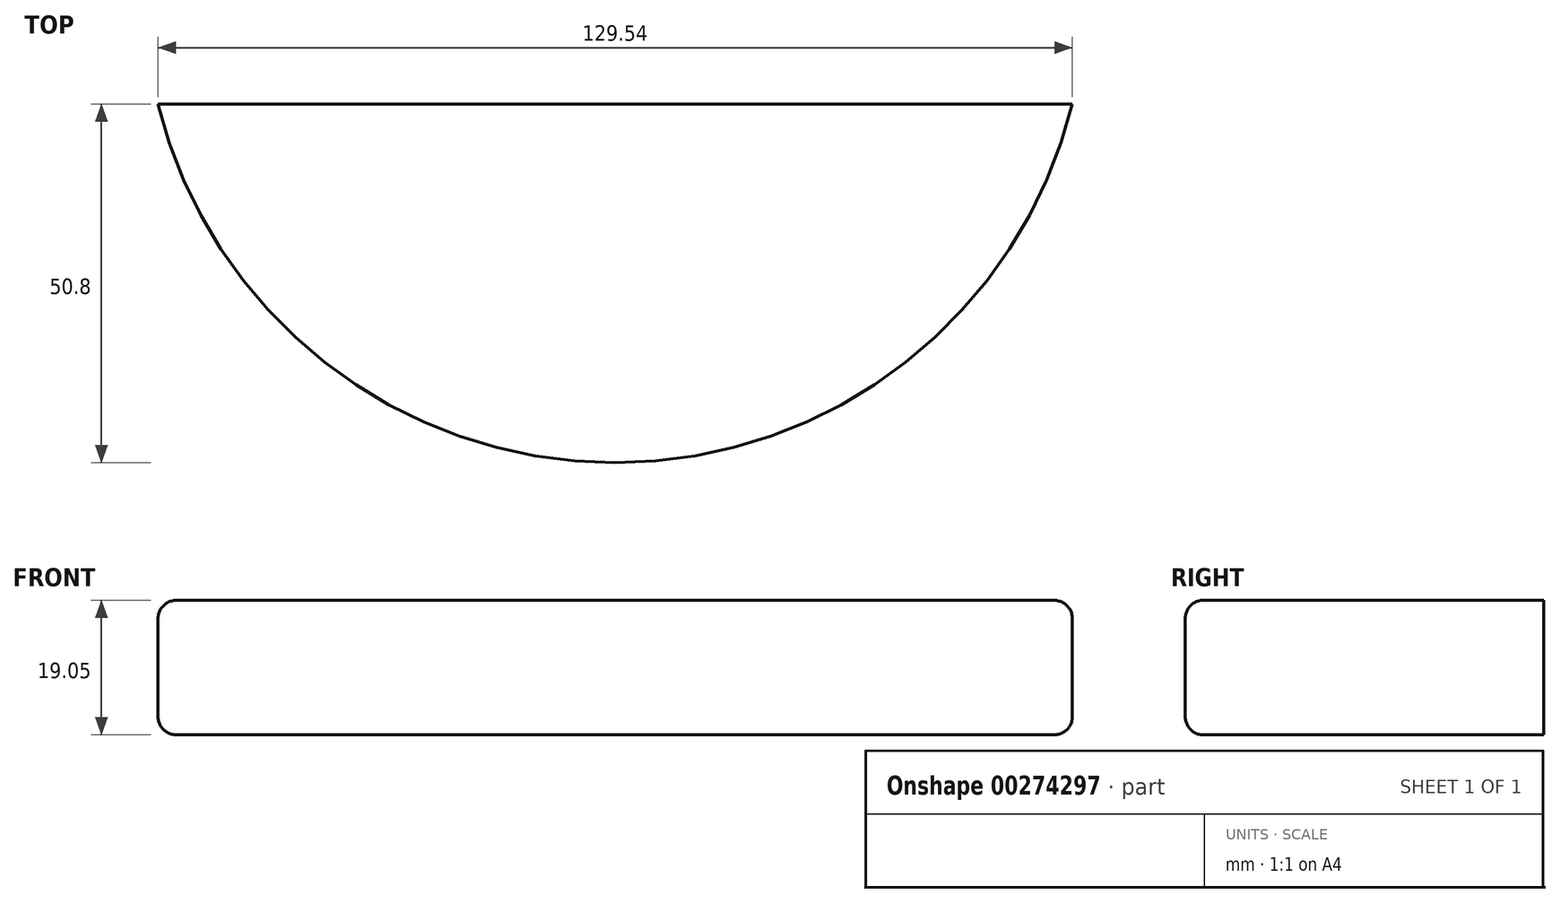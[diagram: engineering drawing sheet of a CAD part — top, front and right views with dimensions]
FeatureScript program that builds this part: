
annotation { "Feature Type Name" : "Feature", "Feature Type Description" : "" }
export const myFeature = defineFeature(function(context is Context, id is Id, definition is map)
    precondition{}
    {
        {
            var Q0;
            Q0=qCreatedBy(makeId("Top.planeOp"),FACE);
            var sketch = newSketch(context, id + "F0", { "sketchPlane" : qUnion([Q0])});
            skLineSegment(sketch, "E0", {"start": v(-48.55, 0) * mm, "end": v(81, 0) * mm});
            skArc(sketch, "E1", {"start": v(-48.55, 0) * mm, "mid": v(16.22, -50.8) * mm, "end": v(81, 0) * mm});
            skSolve(sketch);
        }
        {
            var Q0;
            Q0=makeQuery(id+"F0.imprint","IMPRINT",FACE,{"disambiguationData":[TD([[makeQuery(id+"F0.imprint","IMPRINT",EDGE,{"derivedFrom":sQuery(id+"F0.wireOp",EDGE,"E0")}),-1.0]])]});
            extrude(context, id + "F1", {"entities" : qUnion([Q0]), "depth" : 19.05 * mm});
        }
        {
            var Q0;
            Q0=makeQuery(id+"F1.opExtrude","CAP_EDGE",EDGE,{"disambiguationData":[OSD([sQuery(id+"F0.wireOp",EDGE,"E1")])],"isStart":false});
            var Q1;
            Q1=makeQuery(id+"F1.opExtrude","CAP_EDGE",EDGE,{"disambiguationData":[OSD([sQuery(id+"F0.wireOp",EDGE,"E1")])],"isStart":true});
            fillet(context, id + "F2", {"entities" : qUnion([Q0, Q1]), "radius" : 2.54 * mm, "tangentPropagation" : true, "allowEdgeOverflow" : false});
        }
    });
